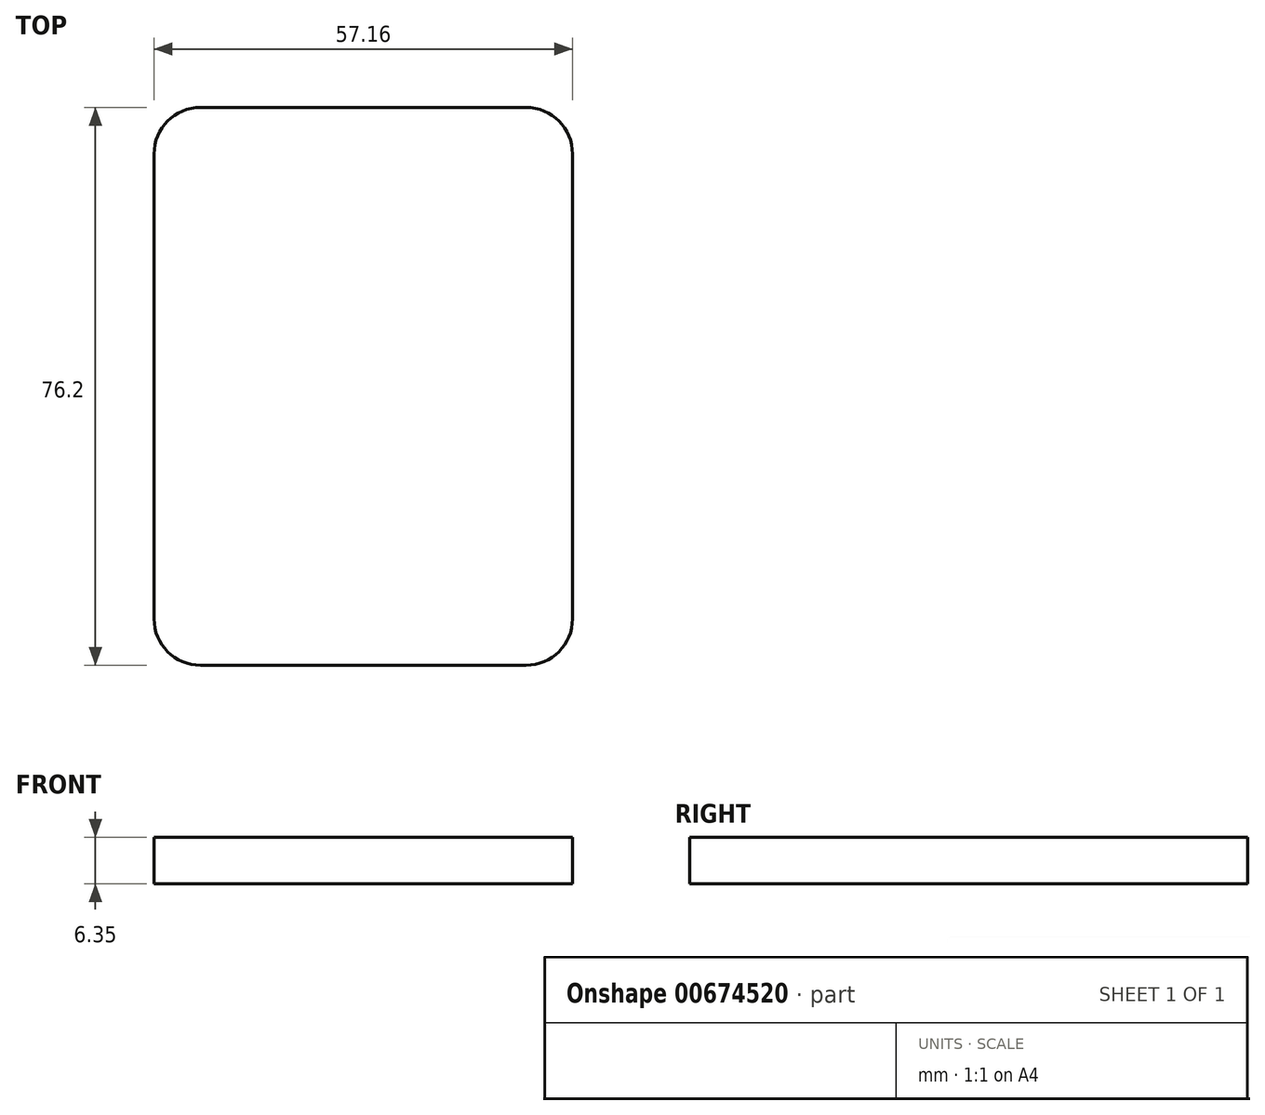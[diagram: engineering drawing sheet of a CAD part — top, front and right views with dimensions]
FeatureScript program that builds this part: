
annotation { "Feature Type Name" : "Feature", "Feature Type Description" : "" }
export const myFeature = defineFeature(function(context is Context, id is Id, definition is map)
    precondition{}
    {
        {
            var Q0;
            Q0=qCreatedBy(makeId("Top.planeOp"),FACE);
            var sketch = newSketch(context, id + "F0", { "sketchPlane" : qUnion([Q0])});
            skLineSegment(sketch, "E0.bottom", {"start": v(22.23, 38.1) * mm, "end": v(-22.23, 38.1) * mm});
            skLineSegment(sketch, "E0.top", {"start": v(22.22, -38.1) * mm, "end": v(-22.22, -38.1) * mm});
            skLineSegment(sketch, "E0.left", {"start": v(28.57, 31.75) * mm, "end": v(28.57, -31.75) * mm});
            skLineSegment(sketch, "E0.right", {"start": v(-28.58, 31.75) * mm, "end": v(-28.58, -31.75) * mm});
            skPoint(sketch, "E0.middle", {"position": v(0, 0) * mm});
            skPoint(sketch, "E1.visualSharp", {"position": v(28.58, 38.1) * mm});
            skArc(sketch, "E1.filletArc", {"start": v(28.58, 31.75) * mm, "mid": v(26.72, 36.24) * mm, "end": v(22.23, 38.1) * mm});
            skPoint(sketch, "E2.visualSharp", {"position": v(28.57, -38.1) * mm});
            skArc(sketch, "E2.filletArc", {"start": v(22.22, -38.1) * mm, "mid": v(26.72, -36.24) * mm, "end": v(28.57, -31.75) * mm});
            skPoint(sketch, "E3.visualSharp", {"position": v(-28.57, -38.1) * mm});
            skArc(sketch, "E3.filletArc", {"start": v(-28.58, -31.75) * mm, "mid": v(-26.72, -36.24) * mm, "end": v(-22.23, -38.1) * mm});
            skPoint(sketch, "E4.visualSharp", {"position": v(-28.58, 38.1) * mm});
            skArc(sketch, "E4.filletArc", {"start": v(-22.23, 38.1) * mm, "mid": v(-26.72, 36.24) * mm, "end": v(-28.58, 31.75) * mm});
            skSolve(sketch);
        }
        {
            var Q0;
            Q0 = qSketchRegion(id + "F0", true);
            extrude(context, id + "F1", {"entities" : qUnion([Q0]), "depth" : 6.35 * mm, "offsetDistance" : 25.4 * mm});
        }
    });
